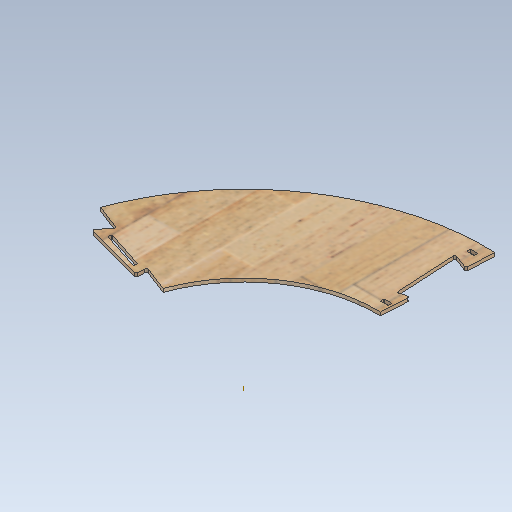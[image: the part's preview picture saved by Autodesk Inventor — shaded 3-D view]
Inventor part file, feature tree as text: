
AUTODESK INVENTOR PART (.ipt)
format: ipt  version: 2020 (Build 240168000, 168)  size: 467,456 bytes
history: native  units: mm
features: extrude x5, sketch x4, pattern_circular x3, mirror x2
ambient origin geometry x8: Origin, YZ Plane, XZ Plane, XY Plane, X Axis, Y Axis, Z Axis, Center Point
bodies: Body1 (feature_tree)
feature tree (14):
  extrude  "Extrusion3"  Depth=6.5mm
  extrude  "Extrusion4"  Depth=2.666667mm
  sketch  "Sketch3"  dims[d24=2.666667mm d25=2.666667mm]
  sketch  "Sketch5"  dims[d32=1.333333mm d33=1.333333mm]
  extrude  "Extrusion7"  Depth=1.333333mm
  pattern_circular  "Circular Pattern2"  [2 undecoded]
  pattern_circular  "Circular Pattern3"  [2 undecoded]
  mirror  "Mirror3"
  extrude  "Extrusion10"  Depth=70.0mm
  mirror  "Mirror4"
  pattern_circular  "Circular Pattern4"  [2 undecoded]
  extrude  "Extrusion11"  Depth=2.666667mm
  sketch  "Sketch2"  dims[d15=6.0mm d16=0.0mm d21=6.5mm]
  sketch  "Sketch6"  dims[d38=0.0mm d39=0.0mm d40=3.25mm d52=4.363323mm d60=0.872665mm d61=12.566371mm d62=13.439035mm d63=2.666667mm d64=0.523599mm d66=0.523599mm d67=2.666667mm d68=2.666667mm d70=12.566371mm d71=12.566371mm d84=467.42mm d85=850.0mm d86=658.71mm d87=150.07mm d88=425.0mm d89=4.363323mm d90=1.919862mm d91=1.919862mm d104=6.5mm d105=12.0mm d108=1.333333mm d109=1.333333mm d110=1.333333mm d111=1.333333mm d112=0.0mm d113=0.0mm d114=0.0mm d145=20.0mm d146=12.566371mm d149=145.0mm d150=90.0deg d151=90.0deg d152=90.0deg d153=90.0deg d154=20.0mm d155=25.132741mm d157=10.0mm d158=0.0mm d162=70.0mm d163=294.355mm d165=3.25mm d174=20.0mm d175=25.132741mm d177=0.0mm d178=0.0mm d176=0.5mm]
note: 6 required parameter values undecoded (feature->parameter linkage not recoverable at this tier; creation-order binding heuristic only, values carry confidence <= 0.55)
